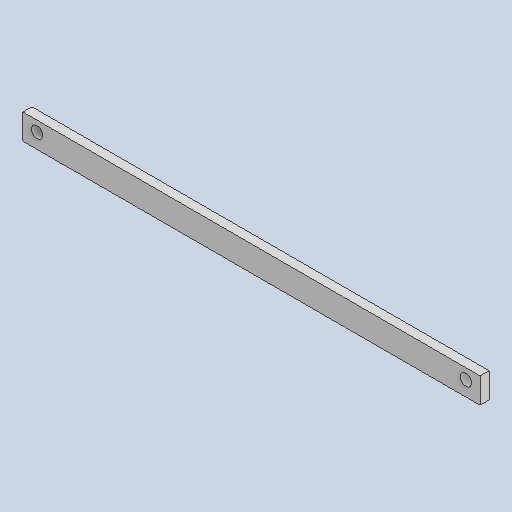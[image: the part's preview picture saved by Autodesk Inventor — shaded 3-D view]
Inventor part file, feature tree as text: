
AUTODESK INVENTOR PART (.ipt)
format: ipt  version: 2022 (Build 260153000, 153)  size: 111,104 bytes
history: native  units: mm
features: reference x11, other x3, extrude x1, sketch x1
ambient origin geometry x8: Origin, YZ Plane, XZ Plane, XY Plane, X Axis, Y Axis, Z Axis, Center Point
bodies: Solid1 (feature_tree)
feature tree (16):
  extrude  "Extrusion1"  Depth=9.0mm
  sketch  "Sketch1"  dims[d0=162.0mm d1=9.0mm d2=4.0mm d3=3.7mm d5=3.2mm d6=0.0mm]
  reference  "Reference1"
  reference  "Reference2"
  reference  "Reference3"
  reference  "Reference4"
  reference  "Reference5"
  reference  "Reference6"
  reference  "Reference7"
  reference  "Reference8"
  reference  "Reference9"
  reference  "Reference10"
  reference  "Reference11"
  other  "Caja_Reductora.iam"
  other  "Carcasa_CajaR_Lateral1:1"
  other  "Rodamiento_Ejes:8"
